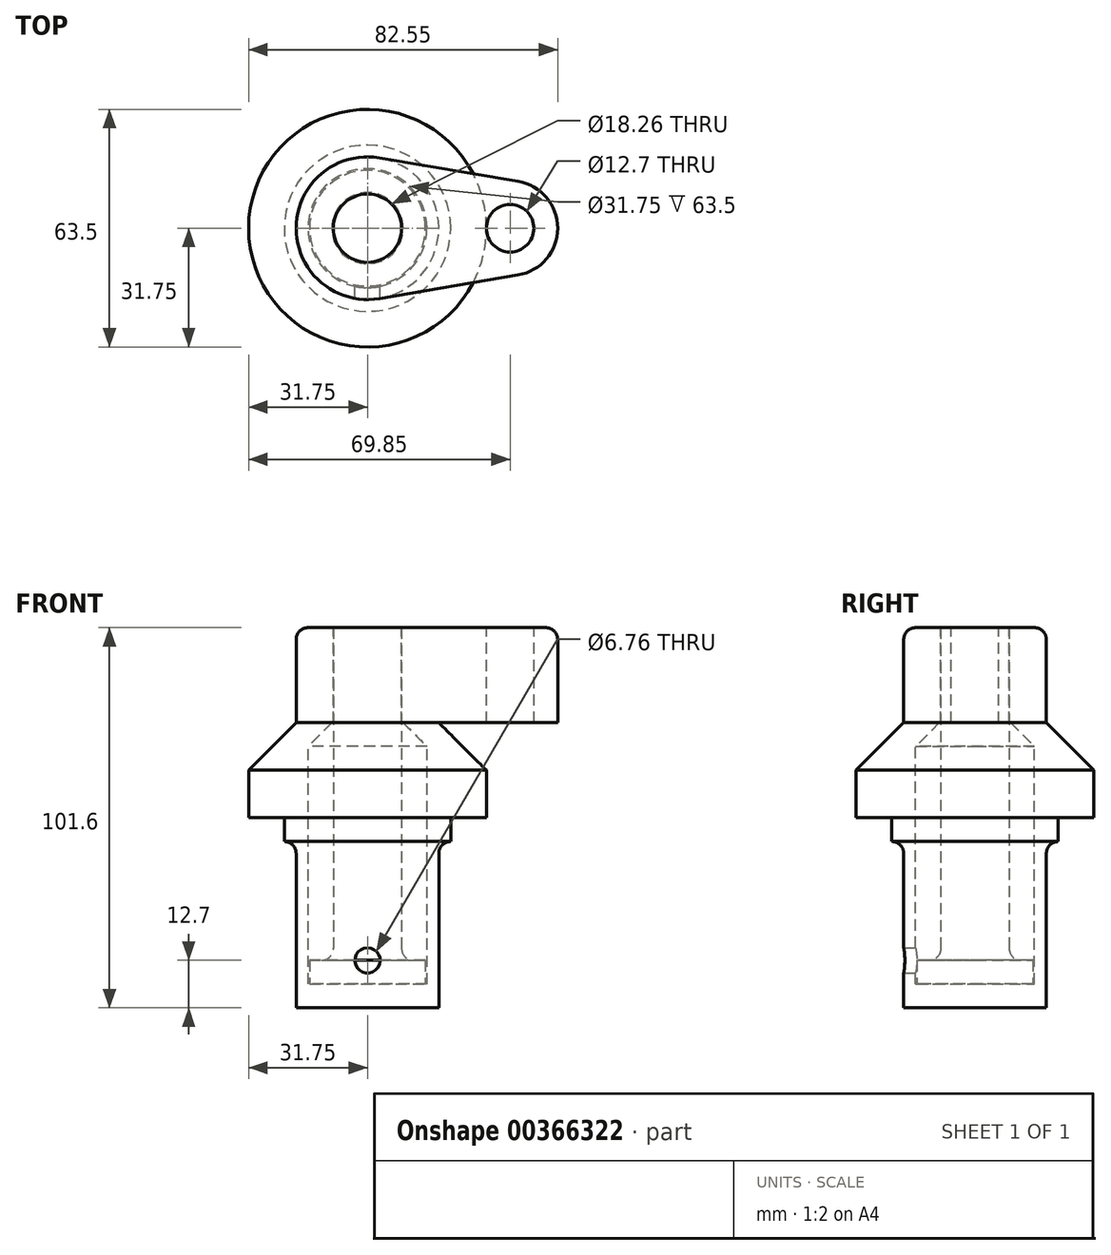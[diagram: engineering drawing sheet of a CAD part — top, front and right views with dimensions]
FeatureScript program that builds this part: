
annotation { "Feature Type Name" : "Feature", "Feature Type Description" : "" }
export const myFeature = defineFeature(function(context is Context, id is Id, definition is map)
    precondition{}
    {
        {
            var Q0;
            Q0=qCreatedBy(makeId("Front.planeOp"),FACE);
            var sketch = newSketch(context, id + "F0", { "sketchPlane" : qUnion([Q0])});
            skLineSegment(sketch, "E0", {"start": v(0, 0) * mm, "end": v(19.05, 0) * mm});
            skLineSegment(sketch, "E1", {"start": v(19.05, 0) * mm, "end": v(19.05, 44.45) * mm});
            skLineSegment(sketch, "E2", {"start": v(19.05, 44.45) * mm, "end": v(22.23, 44.45) * mm});
            skLineSegment(sketch, "E3", {"start": v(22.22, 44.45) * mm, "end": v(22.22, 50.8) * mm});
            skLineSegment(sketch, "E4", {"start": v(22.22, 50.8) * mm, "end": v(31.75, 50.8) * mm});
            skLineSegment(sketch, "E5", {"start": v(31.75, 50.8) * mm, "end": v(31.75, 63.5) * mm});
            skLineSegment(sketch, "E6", {"start": v(31.75, 63.5) * mm, "end": v(19.05, 76.2) * mm});
            skLineSegment(sketch, "E7", {"start": v(19.05, 76.2) * mm, "end": v(0, 76.2) * mm});
            skLineSegment(sketch, "E8", {"start": v(0, 76.2) * mm, "end": v(0, 0) * mm});
            skLineSegment(sketch, "E9", {"start": v(9.52, 76.2) * mm, "end": v(15.87, 69.85) * mm});
            skLineSegment(sketch, "E10", {"start": v(15.87, 69.85) * mm, "end": v(15.87, 6.35) * mm});
            skLineSegment(sketch, "E11", {"start": v(15.87, 6.35) * mm, "end": v(0, 6.35) * mm});
            skLineSegment(sketch, "E12", {"start": v(0, 76.2) * mm, "end": v(0, 88.7) * mm, "construction": true});
            skLineSegment(sketch, "E13", {"start": v(0, 76.2) * mm, "end": v(0, 101.6) * mm});
            skLineSegment(sketch, "E14", {"start": v(0, 101.6) * mm, "end": v(9.13, 101.6) * mm});
            skLineSegment(sketch, "E15", {"start": v(9.13, 101.6) * mm, "end": v(9.13, 12.7) * mm});
            skLineSegment(sketch, "E16", {"start": v(9.13, 12.7) * mm, "end": v(15.48, 12.7) * mm});
            skLineSegment(sketch, "E17", {"start": v(15.48, 12.7) * mm, "end": v(15.48, 6.35) * mm});
            skSolve(sketch);
        }
        {
            var Q0;
            {var subQ1=sQuery(id+"F0.wireOp",EDGE,"E0");Q0=makeQuery(id+"F0.imprint","IMPRINT",FACE,{"disambiguationData":[TD([[makeQuery(id+"F0.imprint","IMPRINT",EDGE,{"derivedFrom":subQ1}),1.0]])]});}
            var Q1;
            Q1=sQuery(id+"F0.wireOp",EDGE,"E8");
            revolve(context, id + "F1", {"entities" : qUnion([Q0]), "axis" : qUnion([Q1]), "revolveType" : RevolveType.FULL});
        }
        {
            var Q0;
            {var subQ0=sQuery(id+"F0.wireOp",EDGE,"E13");Q0=makeQuery(id+"F0.imprint","IMPRINT",FACE,{"disambiguationData":[TD([[makeQuery(id+"F0.imprint","IMPRINT",EDGE,{"derivedFrom":subQ0}),-1.0]])]});}
            var Q1;
            {var subQ6=sQuery(id+"F0.wireOp",EDGE,"E16");Q1=makeQuery(id+"F0.imprint","IMPRINT",FACE,{"disambiguationData":[TD([[makeQuery(id+"F0.imprint","IMPRINT",EDGE,{"derivedFrom":subQ6}),-1.0]])]});}
            var Q2;
            Q2=sQuery(id+"F0.wireOp",EDGE,"E13");
            revolve(context, id + "F2", {"entities" : qUnion([Q0, Q1]), "axis" : qUnion([Q2]), "revolveType" : RevolveType.FULL});
        }
        {
            var Q0;
            Q0=makeQuery(id+"F2.opRevolve","SWEPT_FACE",FACE,{"disambiguationData":[OSD([sQuery(id+"F0.wireOp",EDGE,"E14")])]});
            var sketch = newSketch(context, id + "F3", { "sketchPlane" : qUnion([Q0])});
            skCircle(sketch, "E18", {"center": v(0, 0) * mm, "radius": 19.05 * mm});
            skCircle(sketch, "E19", {"center": v(38.1, 0) * mm, "radius": 12.7 * mm});
            skLineSegment(sketch, "E20", {"start": v(40.22, -12.52) * mm, "end": v(3.17, -18.78) * mm});
            skLineSegment(sketch, "E21", {"start": v(40.22, 12.52) * mm, "end": v(3.17, 18.78) * mm});
            skCircle(sketch, "E22.0", {"center": v(0, 0) * mm, "radius": 9.13 * mm});
            skCircle(sketch, "E23", {"center": v(38.1, 0) * mm, "radius": 6.35 * mm});
            skSolve(sketch);
        }
        {
            var Q0;
            Q0 = qSketchRegion(id + "F3", true);
            var Q1;
            Q1=makeQuery(id+"F1.opRevolve","SWEPT_FACE",FACE,{"disambiguationData":[OSD([sQuery(id+"F0.wireOp",EDGE,"E7")])]});
            extrude(context, id + "F4", {"entities" : qUnion([Q0]), "oppositeDirection" : true, "endBoundEntityFace" : qUnion([Q1]), "depth" : 25.4 * mm});
        }
        {
            var Q0;
            Q0=qCreatedBy(makeId("Front.planeOp"),FACE);
            var sketch = newSketch(context, id + "F5", { "sketchPlane" : qUnion([Q0])});
            skPoint(sketch, "E24", {"position": v(0, 12.7) * mm});
            skSolve(sketch);
        }
        {
            var Q0;
            Q0=sQuery(id+"F5.wireOp",VERTEX,"E24");
            var Q1;
            Q1=makeQuery(id+"F1.opRevolve","SWEPT_BODY",BODY,{"disambiguationData":[OSD([sQuery(id+"F0.wireOp",EDGE,"E0"),sQuery(id+"F0.wireOp",EDGE,"E1"),sQuery(id+"F0.wireOp",EDGE,"E2"),sQuery(id+"F0.wireOp",EDGE,"E3"),sQuery(id+"F0.wireOp",EDGE,"E4"),sQuery(id+"F0.wireOp",EDGE,"E5"),sQuery(id+"F0.wireOp",EDGE,"E6"),sQuery(id+"F0.wireOp",EDGE,"E7"),sQuery(id+"F0.wireOp",EDGE,"E8"),sQuery(id+"F0.wireOp",EDGE,"E9"),sQuery(id+"F0.wireOp",EDGE,"E10"),sQuery(id+"F0.wireOp",EDGE,"E11")])]});
            hole(context, id + "F6", {"style" : HoleStyle.SIMPLE, "endStyle" : HoleEndStyle.THROUGH, "oppositeDirection" : true, "standardTappedOrClearance" : lookupTablePath({ "standard" : "ANSI", "fit" : "Normal (ASME)", "size" : "1/4", "type" : "Clearance" }), "standardBlindInLast" : lookupTablePath({ "fit" : "Free", "standard" : "ANSI", "size" : "1/4", "type" : "Clearance" }), "holeDiameter" : 6.76 * mm, "isTappedThrough" : true, "tappedDepth" : 8.9 * mm, "tapClearance" : 3, "locations" : qUnion([Q0]), "scope" : qUnion([Q1])});
        }
        {
            var Q0;
            Q0=makeQuery(id+"F4.opExtrude","CAP_EDGE",EDGE,{"disambiguationData":[OSD([sQuery(id+"F3.wireOp",EDGE,"E21")])],"isStart":true});
            var Q1;
            Q1=makeQuery(id+"F1.opRevolve","SWEPT_EDGE",EDGE,{"disambiguationData":[OSD([sQuery(id+"F0.wireOp",EDGE,"E1"),sQuery(id+"F0.wireOp",EDGE,"E2")])]});
            var Q2;
            Q2=makeQuery(id+"F2.opRevolve","SWEPT_EDGE",EDGE,{"disambiguationData":[OSD([sQuery(id+"F0.wireOp",EDGE,"E15"),sQuery(id+"F0.wireOp",EDGE,"E16")])]});
            fillet(context, id + "F7", {"entities" : qUnion([Q0, Q1, Q2]), "radius" : 3.17 * mm, "tangentPropagation" : true, "allowEdgeOverflow" : false});
        }
    });
